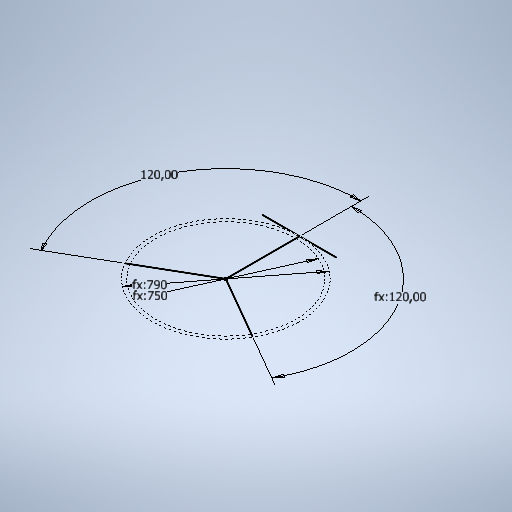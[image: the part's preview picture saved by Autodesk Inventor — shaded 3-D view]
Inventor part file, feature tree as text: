
AUTODESK INVENTOR PART (.ipt)
format: ipt  version: 2025.4 (Build 294407000, 407)  size: 256,000 bytes
history: native  units: mm
features: sketch x1
ambient origin geometry x8: Origin, YZ Plane, XZ Plane, XY Plane, X Axis, Y Axis, Z Axis, Center Point
feature tree (1):
  sketch  "Sketch1"  dims[d1=750.0mm d2=120.0deg d3=120.0deg d4=790.0mm]
